# Revit family: Lighting_Emergency&Security_Luznor_G-Led-watertight-IP65_ESP
name_source: partatom
category: Lighting Fixtures
revit_build: Autodesk Revit 2018 (Build: 20190510_1515(x64)
units: mm (PartAtom-declared; Revit-internal decimal feet)

## family parameters
Cut with Voids When Loaded = No
Host = Face
Light Source = Yes
OmniClass Number = 23.35.47.13
OmniClass Title = Emergency Lighting
Part Type = Normal
Room Calculation Point = No
Round Connector Dimension = Use Diameter
Shared = No

## types (1)
- G Led watertight (IP65)
    Altura = 142 mm  [stored 0.465879 ft]
    Anchura = 322 mm  [stored 1.05643 ft]
    Apparent Load = 0 VA
    BIMobject category = Emergency & Security
    Color Filter = 16777215
    Default Elevation = 1219 mm
    Description = Máxima eficiencia. La Serie G-Led incorpora tecnología LED que proporciona una iluminación homogénea y de calidad a sus modelos permanentes y no permanentes.G Led se diferencia por su novedoso difusor interno diseñado para evitar el contacto visual directo con la fuente de luz. Integra iluminación de cortesía por medio de tres leds.
Características
 IP-65 Envolvente 100% policarbonato con difusor transparente de serie u opal suave o fuerte Difusor interno 100% policarbonato, transparente de serie, opcional opal suave o fuerte Tecnología LED Sistema de Protección Ocular (SPO) Baterías Ni-Cd de alta temperatura Eficiencia energética Montaje en superficie
    Design country = Spain
    Dimming Lamp Color Temperature Shift = <None>
    Edition number = 1
    Emit Shape Visible in Rendering = No
    Emit from Rectangle Length = 322 mm  [stored 1.05643 ft]
    Emit from Rectangle Width = 142 mm  [stored 0.465879 ft]
    Especificación técnica = Color: Blanco frío (5.000 K) Flujo en emergencia (lm): 110 - 580 Flujo en presencia de red (lm): 110 - 580 Indicador de carga: 1 x LED verde Autonomía (h): 1-2-3 Fuente de alimentación: 110 Vac - 230 Vac - 50/60 Hz Telemandable: Si (TL-300) Índice de protección: IP65 - IK04 Aislamiento eléctrico: Clase II Normativa: Marcado CE (93/68/EEC): 2014/35/UE, 2014/30/UE and 2011/65/UE
    Horas de autonomía = Autonomía : 1 hora
    IFC Classification = Lamp
    Información difusor = El difusor se puede solicitar en 3 acabados diferentes: transparente (paso del 100% de la luz), opal suave (paso del 92% de la luz), u ópalo fuerte (paseo del 72% de la luz)
    Intensidad luminosa = Revisar por favor el link en la descripción técnica para comprobar las diferentes opciones ofrecidas por el fabricante
    Lamp = LED
    Manufacturer = Luznor
    Manufacturer country = Spain
    Manufacturer name = Luznor
    Masterformat 2014 Code = 26 52 00
    Masterformat 2014 Description = Emergency Lighting
    Material caja = Luznor - Plástico - Blanco
    Material main = Polycarbonate
    Material marco = Luznor - Plástico - Blanco
    Material secondary = Electronic & optical components
    Model = G Led watertight (IP65)
    NBS Reference Code = 70-50-74
    NBS Reference Description = Self-Contained Emergency Luminaires
    OmniClass Code = 23-35 47 13
    OmniClass Description = Emergency Lighting
    Photometric Web File = GLed.IES
    Product Guid = de2e1557-58c0-42e2-b79e-91cc08812470
    Product SKU = g-led-IP65
    Product data url = https://bimobject.com
    Product family = G Series
    Product group = G Led
    Product name = G Led watertight (IP65)
    Product url = https://www.luznor.com
    Profundidad = 74 mm
    QR code = https://bimobject.com
    Tilt Angle = -90.00°
    UNSPSC Code = 391117
    URL = https://www.luznor.com
    Uniclass 1.4 Code = JV55
    Uniclass 1.4 Description = Self contained emergency and signage systems
    Uniclass 2.0 Code = PR-70-50-74
    Uniclass 2.0 Description = Self-Contained Emergency Luminaires
    Uniclass 2015 Code = Pr_70_70_48_77
    Uniclass 2015 Name = Self-contained emergency luminaires
    Uniformat II Code = D5020
    Uniformat II Description = Lighting & Branch Wiring

note: [stored X ft] marks values corroborated as IEEE doubles in the binary element streams (Revit-internal decimal feet)

## geometry (parser evidence)
native form markers: Sweep x6
no freeform markers — native parametric forms only
